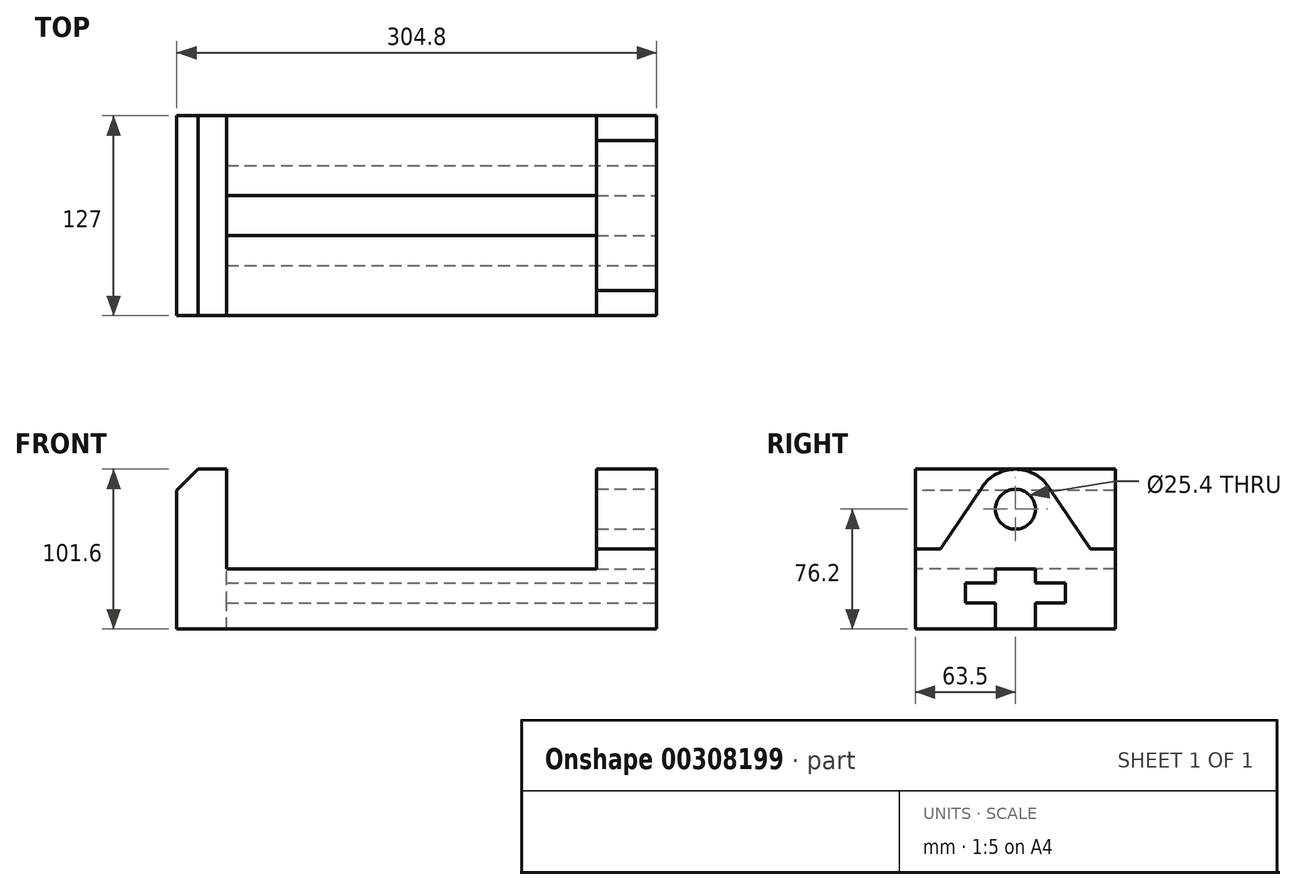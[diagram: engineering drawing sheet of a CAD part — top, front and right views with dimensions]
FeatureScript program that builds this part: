
annotation { "Feature Type Name" : "Feature", "Feature Type Description" : "" }
export const myFeature = defineFeature(function(context is Context, id is Id, definition is map)
    precondition{}
    {
        {
            var Q0;
            Q0=qCreatedBy(makeId("Front.planeOp"),FACE);
            var sketch = newSketch(context, id + "F0", { "sketchPlane" : qUnion([Q0])});
            skLineSegment(sketch, "E0", {"start": v(0, 0) * mm, "end": v(0, 88.13) * mm});
            skLineSegment(sketch, "E1", {"start": v(0, 88.13) * mm, "end": v(13.47, 101.6) * mm});
            skLineSegment(sketch, "E2", {"start": v(13.47, 101.6) * mm, "end": v(31.75, 101.6) * mm});
            skLineSegment(sketch, "E3", {"start": v(31.75, 101.6) * mm, "end": v(31.75, 38.1) * mm});
            skLineSegment(sketch, "E4", {"start": v(31.75, 38.1) * mm, "end": v(266.7, 38.1) * mm});
            skLineSegment(sketch, "E5", {"start": v(266.7, 38.1) * mm, "end": v(266.7, 101.6) * mm});
            skLineSegment(sketch, "E6", {"start": v(266.7, 101.6) * mm, "end": v(304.8, 101.6) * mm});
            skLineSegment(sketch, "E7", {"start": v(304.8, 101.6) * mm, "end": v(304.8, 0) * mm});
            skLineSegment(sketch, "E8", {"start": v(304.8, 0) * mm, "end": v(0, 0) * mm});
            skSolve(sketch);
        }
        {
            var Q0;
            Q0 = qSketchRegion(id + "F0", true);
            extrude(context, id + "F1", {"entities" : qUnion([Q0]), "oppositeDirection" : true, "depth" : 127 * mm});
        }
        {
            var Q0;
            Q0=makeQuery(id+"F1.opExtrude","SWEPT_FACE",FACE,{"disambiguationData":[OSD([sQuery(id+"F0.wireOp",EDGE,"E7")])]});
            var sketch = newSketch(context, id + "F2", { "sketchPlane" : qUnion([Q0])});
            skLineSegment(sketch, "E9", {"start": v(50.8, 0) * mm, "end": v(50.8, 16.5) * mm});
            skLineSegment(sketch, "E10", {"start": v(50.8, 16.5) * mm, "end": v(31.75, 16.5) * mm});
            skLineSegment(sketch, "E11", {"start": v(31.75, 16.5) * mm, "end": v(31.75, 29.2) * mm});
            skLineSegment(sketch, "E12", {"start": v(31.75, 29.2) * mm, "end": v(50.8, 29.2) * mm});
            skLineSegment(sketch, "E13", {"start": v(50.8, 29.2) * mm, "end": v(50.8, 38.1) * mm});
            skLineSegment(sketch, "E14", {"start": v(50.8, 38.1) * mm, "end": v(76.2, 38.1) * mm});
            skLineSegment(sketch, "E15", {"start": v(76.2, 38.1) * mm, "end": v(76.2, 29.2) * mm});
            skLineSegment(sketch, "E16", {"start": v(76.2, 29.2) * mm, "end": v(95.25, 29.2) * mm});
            skLineSegment(sketch, "E17", {"start": v(95.25, 29.2) * mm, "end": v(95.25, 16.5) * mm});
            skLineSegment(sketch, "E18", {"start": v(95.25, 16.5) * mm, "end": v(76.2, 16.5) * mm});
            skLineSegment(sketch, "E19", {"start": v(76.2, 16.5) * mm, "end": v(76.2, 0) * mm});
            skLineSegment(sketch, "E20", {"start": v(63.5, 101.6) * mm, "end": v(63.5, 0) * mm, "construction": true});
            skSolve(sketch);
        }
        {
            var Q0;
            {var subQ0=sQuery(id+"F2.wireOp",EDGE,"E9");Q0=makeQuery(id+"F2.imprint","IMPRINT",FACE,{"disambiguationData":[TD([[makeQuery(id+"F2.imprint","IMPRINT",EDGE,{"derivedFrom":subQ0}),-1.0]])]});}
            extrude(context, id + "F3", {"entities" : qUnion([Q0]), "operationType" : NewBodyOperationType.REMOVE, "oppositeDirection" : true, "depth" : 273.05 * mm});
        }
        {
            var Q0;
            Q0=makeQuery(id+"F1.opExtrude","SWEPT_FACE",FACE,{"disambiguationData":[OSD([sQuery(id+"F0.wireOp",EDGE,"E7")])]});
            var sketch = newSketch(context, id + "F4", { "sketchPlane" : qUnion([Q0])});
            skLineSegment(sketch, "E21", {"start": v(63.5, 101.6) * mm, "end": v(63.5, 0) * mm, "construction": true});
            skLineSegment(sketch, "E22", {"start": v(0, 50.8) * mm, "end": v(15.88, 50.8) * mm});
            skLineSegment(sketch, "E23", {"start": v(127, 50.8) * mm, "end": v(111.12, 50.8) * mm});
            skCircle(sketch, "E24", {"center": v(63.5, 76.2) * mm, "radius": 12.7 * mm});
            skLineSegment(sketch, "E25", {"start": v(15.87, 50.8) * mm, "end": v(42.4, 90.35) * mm});
            skLineSegment(sketch, "E26", {"start": v(111.13, 50.8) * mm, "end": v(84.6, 90.35) * mm});
            skArc(sketch, "E27", {"start": v(84.6, 90.35) * mm, "mid": v(63.5, 101.6) * mm, "end": v(42.4, 90.35) * mm});
            skSolve(sketch);
        }
        {
            var Q0;
            Q0=makeQuery(id+"F4.imprint","IMPRINT",FACE,{"disambiguationData":[TD([[makeQuery(id+"F4.imprint","IMPRINT",EDGE,{"derivedFrom":sQuery(id+"F4.wireOp",EDGE,"E24")}),1.0]])]});
            extrude(context, id + "F5", {"entities" : qUnion([Q0]), "operationType" : NewBodyOperationType.REMOVE, "oppositeDirection" : true, "depth" : 50.8 * mm});
        }
        {
            var Q0;
            {var subQ7=sQuery(id+"F4.wireOp",EDGE,"E22");Q0=makeQuery(id+"F4.imprint","IMPRINT",FACE,{"disambiguationData":[TD([[makeQuery(id+"F4.imprint","IMPRINT",EDGE,{"derivedFrom":subQ7}),1.0]])]});}
            var Q1;
            {var subQ7=sQuery(id+"F4.wireOp",EDGE,"E23");Q1=makeQuery(id+"F4.imprint","IMPRINT",FACE,{"disambiguationData":[TD([[makeQuery(id+"F4.imprint","IMPRINT",EDGE,{"derivedFrom":subQ7}),-1.0]])]});}
            extrude(context, id + "F6", {"entities" : qUnion([Q0, Q1]), "operationType" : NewBodyOperationType.REMOVE, "oppositeDirection" : true, "depth" : 50.8 * mm});
        }
    });
